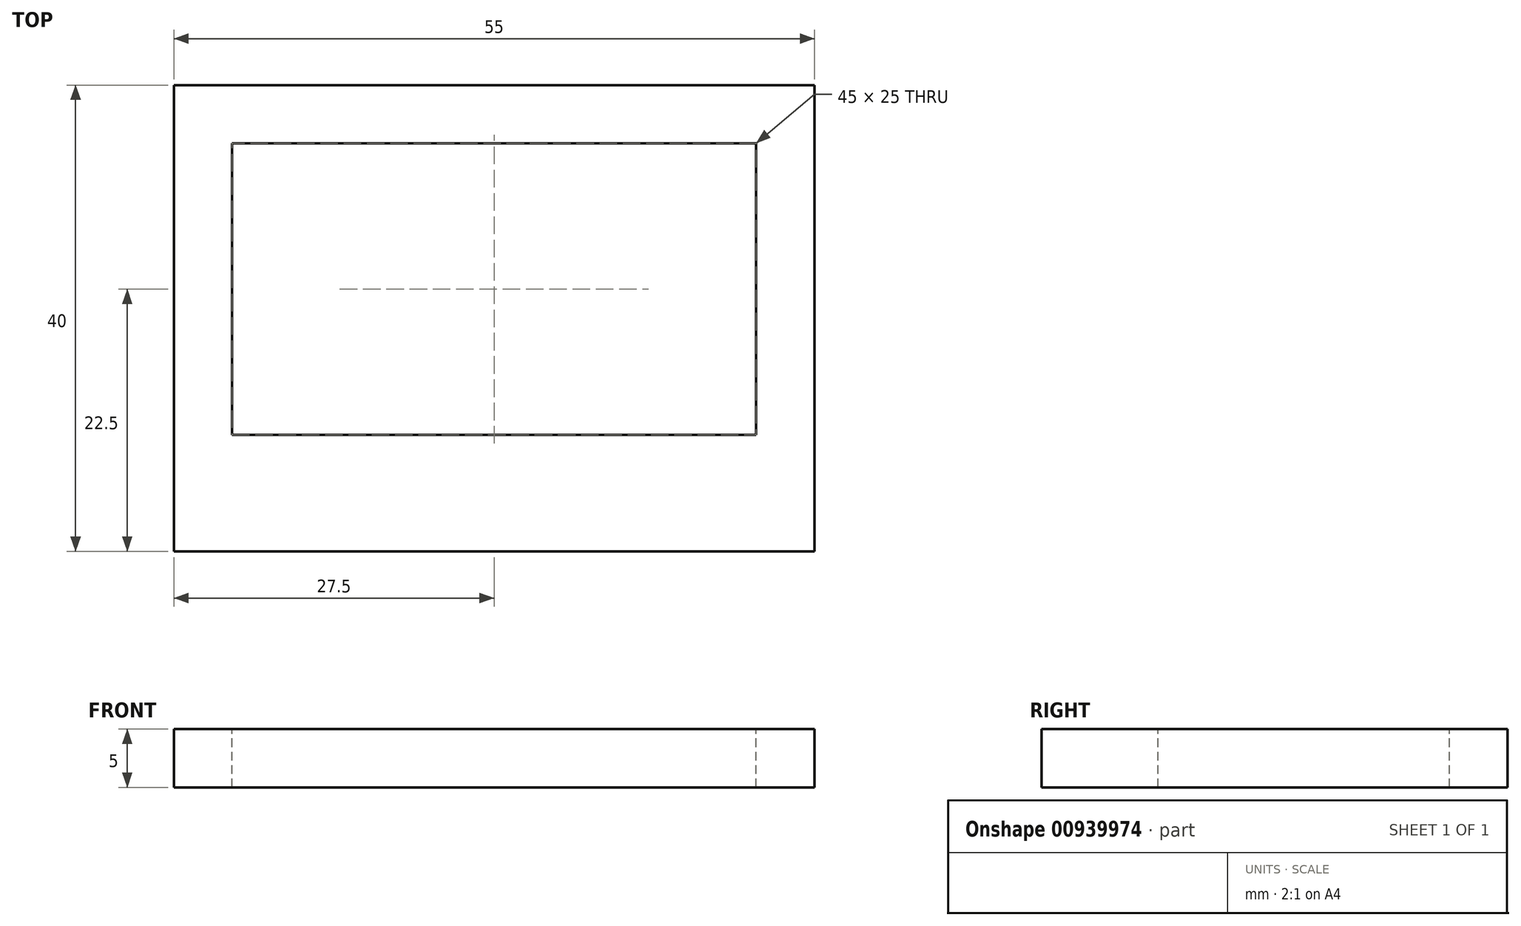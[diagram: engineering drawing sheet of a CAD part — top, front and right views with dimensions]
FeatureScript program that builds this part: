
annotation { "Feature Type Name" : "Feature", "Feature Type Description" : "" }
export const myFeature = defineFeature(function(context is Context, id is Id, definition is map)
    precondition{}
    {
        {
            var Q0;
            Q0=qCreatedBy(makeId("Top.planeOp"),FACE);
            var sketch = newSketch(context, id + "F0", { "sketchPlane" : qUnion([Q0])});
            skLineSegment(sketch, "E0.bottom", {"start": v(0, 0) * mm, "end": v(55, 0) * mm});
            skLineSegment(sketch, "E0.top", {"start": v(0, 40) * mm, "end": v(55, 40) * mm});
            skLineSegment(sketch, "E0.left", {"start": v(0, 0) * mm, "end": v(0, 40) * mm});
            skLineSegment(sketch, "E0.right", {"start": v(55, 0) * mm, "end": v(55, 40) * mm});
            skSolve(sketch);
        }
        {
            var Q0;
            Q0=qSketchRegion(id+"F0",true);
            extrude(context, id + "F1", {"entities" : qUnion([Q0]), "depth" : 5 * mm, "offsetDistance" : 25 * mm});
        }
        {
            var Q0;
            Q0=makeQuery(id+"F1.opExtrude","CAP_FACE",FACE,{"disambiguationData":[OSD([sQuery(id+"F0.wireOp",EDGE,"E0.bottom"),sQuery(id+"F0.wireOp",EDGE,"E0.top"),sQuery(id+"F0.wireOp",EDGE,"E0.left"),sQuery(id+"F0.wireOp",EDGE,"E0.right")])],"isStart":false});
            var sketch = newSketch(context, id + "F2", { "sketchPlane" : qUnion([Q0])});
            skLineSegment(sketch, "E1.0", {"start": v(50, 0) * mm, "end": v(50, 35) * mm});
            skLineSegment(sketch, "E1.1", {"start": v(5, 35) * mm, "end": v(50, 35) * mm});
            skLineSegment(sketch, "E1.2", {"start": v(5, 0) * mm, "end": v(5, 35) * mm});
            skLineSegment(sketch, "E2", {"start": v(5, 10) * mm, "end": v(50, 10) * mm});
            skPoint(sketch, "E2.endSnap0", {"position": v(50, 17.5) * mm});
            skSolve(sketch);
        }
        {
            var Q0;
            {var subQ0=sQuery(id+"F2.wireOp",EDGE,"E1.1");Q0=makeQuery(id+"F2.imprint","IMPRINT",FACE,{"disambiguationData":[TD([[makeQuery(id+"F2.imprint","IMPRINT",EDGE,{"derivedFrom":subQ0}),-1.0]])]});}
            extrude(context, id + "F3", {"entities" : qUnion([Q0]), "operationType" : NewBodyOperationType.REMOVE, "endBound" : BoundingType.UP_TO_NEXT, "oppositeDirection" : true, "depth" : 25 * mm, "offsetDistance" : 25 * mm});
        }
    });
